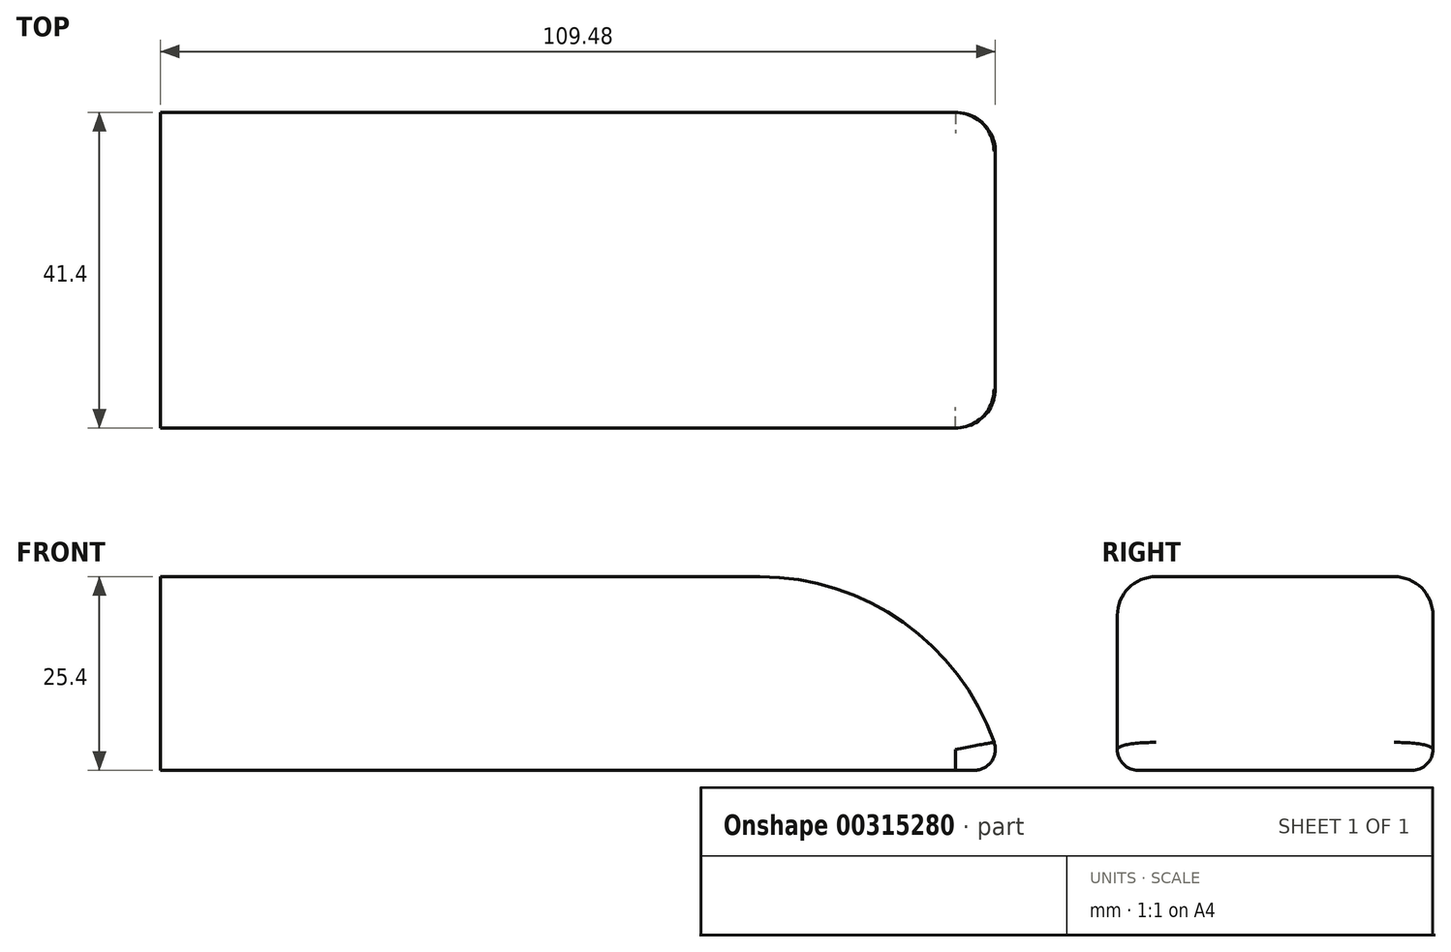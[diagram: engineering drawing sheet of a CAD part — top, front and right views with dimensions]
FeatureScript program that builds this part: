
annotation { "Feature Type Name" : "Feature", "Feature Type Description" : "" }
export const myFeature = defineFeature(function(context is Context, id is Id, definition is map)
    precondition{}
    {
        {
            var Q0;
            Q0=qCreatedBy(makeId("Top.planeOp"),FACE);
            var sketch = newSketch(context, id + "F0", { "sketchPlane" : qUnion([Q0])});
            skLineSegment(sketch, "E0.bottom", {"start": v(55.2, 20.7) * mm, "end": v(-55.2, 20.7) * mm});
            skLineSegment(sketch, "E0.top", {"start": v(55.2, -20.7) * mm, "end": v(-55.2, -20.7) * mm});
            skLineSegment(sketch, "E0.left", {"start": v(55.2, 20.7) * mm, "end": v(55.2, -20.7) * mm});
            skLineSegment(sketch, "E0.right", {"start": v(-55.2, 20.7) * mm, "end": v(-55.2, -20.7) * mm});
            skPoint(sketch, "E0.middle", {"position": v(0, 0) * mm});
            skSolve(sketch);
        }
        {
            var Q0;
            Q0 = qSketchRegion(id + "F0", true);
            extrude(context, id + "F1", {"entities" : qUnion([Q0]), "depth" : 25.4 * mm});
        }
        {
            var Q0;
            Q0=makeQuery(id+"F1.opExtrude","CAP_EDGE",EDGE,{"disambiguationData":[OSD([sQuery(id+"F0.wireOp",EDGE,"E0.left")])],"isStart":false});
            fillet(context, id + "F2", {"entities" : qUnion([Q0]), "radius" : 32.57 * mm, "tangentPropagation" : true, "allowEdgeOverflow" : false});
        }
        {
            var Q0;
            Q0=makeQuery(id+"F1.opExtrude","CAP_EDGE",EDGE,{"disambiguationData":[OSD([sQuery(id+"F0.wireOp",EDGE,"E0.top")])],"isStart":false});
            var Q1;
            Q1=makeQuery(id+"F1.opExtrude","CAP_EDGE",EDGE,{"disambiguationData":[OSD([sQuery(id+"F0.wireOp",EDGE,"E0.bottom")])],"isStart":false});
            fillet(context, id + "F3", {"entities" : qUnion([Q0, Q1]), "radius" : 5.08 * mm, "tangentPropagation" : true, "allowEdgeOverflow" : false});
        }
        {
            var Q0;
            Q0=makeQuery(id+"F1.opExtrude","CAP_EDGE",EDGE,{"disambiguationData":[OSD([sQuery(id+"F0.wireOp",EDGE,"E0.top")])],"isStart":true});
            var Q1;
            Q1=makeQuery(id+"F1.opExtrude","CAP_EDGE",EDGE,{"disambiguationData":[OSD([sQuery(id+"F0.wireOp",EDGE,"E0.bottom")])],"isStart":true});
            fillet(context, id + "F4", {"entities" : qUnion([Q0, Q1]), "radius" : 2.76 * mm, "tangentPropagation" : true, "allowEdgeOverflow" : false});
        }
    });
